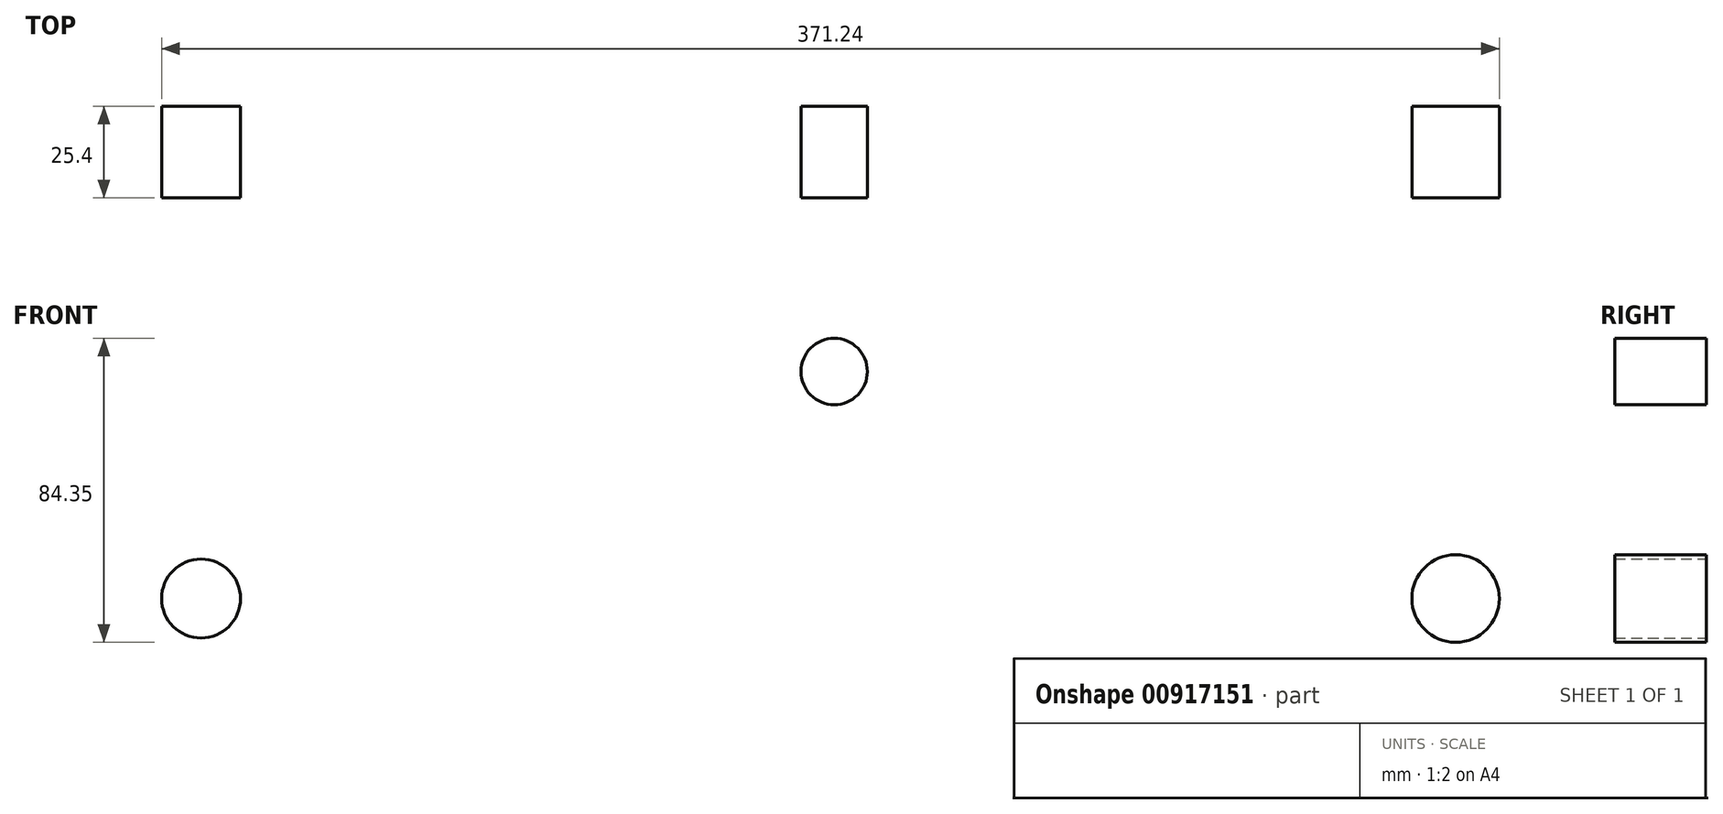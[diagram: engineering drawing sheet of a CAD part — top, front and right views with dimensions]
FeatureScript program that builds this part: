
annotation { "Feature Type Name" : "Feature", "Feature Type Description" : "" }
export const myFeature = defineFeature(function(context is Context, id is Id, definition is map)
    precondition{}
    {
        {
            var Q0;
            Q0=qCreatedBy(makeId("Front.planeOp"),FACE);
            var sketch = newSketch(context, id + "F0", { "sketchPlane" : qUnion([Q0])});
            skCircle(sketch, "E0", {"center": v(0, 0) * mm, "radius": 9.2 * mm});
            skCircle(sketch, "E1", {"center": v(-175.7, -63) * mm, "radius": 10.95 * mm});
            skCircle(sketch, "E2", {"center": v(172.44, -63) * mm, "radius": 12.14 * mm});
            skSolve(sketch);
        }
        {
            var Q0;
            Q0 = qSketchRegion(id + "F0", true);
            extrude(context, id + "F1", {"entities" : qUnion([Q0]), "depth" : 25.4 * mm, "offsetDistance" : 25.4 * mm});
        }
        {
            var Q0;
            Q0=qCreatedBy(makeId("Front.planeOp"),FACE);
            cPlane(context, id + "F2", {"entities" : qUnion([Q0]), "cplaneType" : CPlaneType.OFFSET, "offset" : 10.16 * mm, "width" : 152.4 * mm, "height" : 152.4 * mm});
        }
    });
